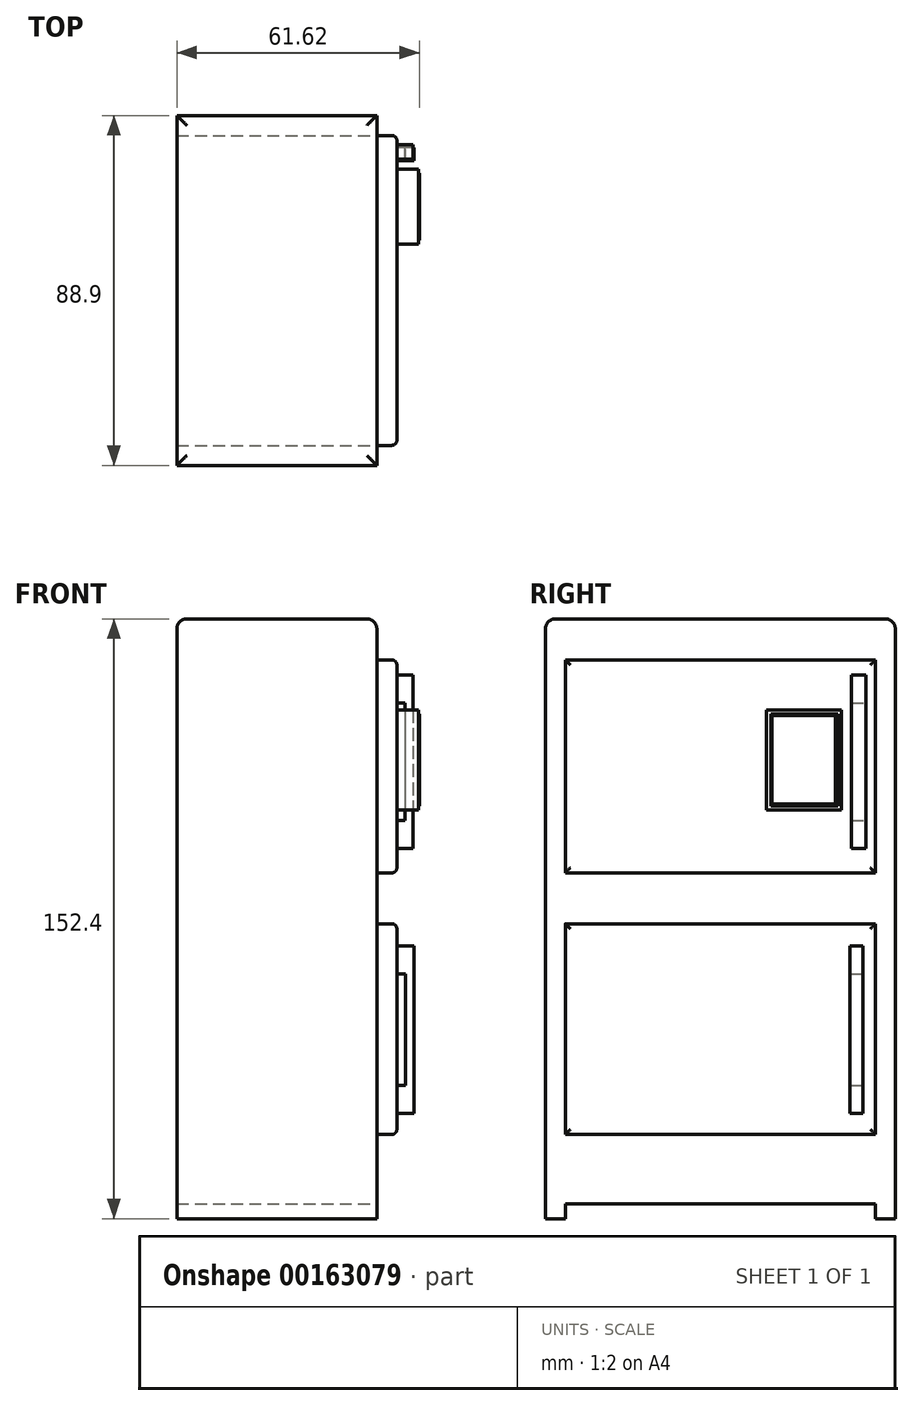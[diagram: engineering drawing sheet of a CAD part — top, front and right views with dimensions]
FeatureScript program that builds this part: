
annotation { "Feature Type Name" : "Feature", "Feature Type Description" : "" }
export const myFeature = defineFeature(function(context is Context, id is Id, definition is map)
    precondition{}
    {
        {
            var Q0;
            Q0=qCreatedBy(makeId("Top.planeOp"),FACE);
            var sketch = newSketch(context, id + "F0", { "sketchPlane" : qUnion([Q0])});
            skLineSegment(sketch, "E0.bottom", {"start": v(0, 0) * mm, "end": v(50.8, 0) * mm});
            skLineSegment(sketch, "E0.top", {"start": v(0, -88.9) * mm, "end": v(50.8, -88.9) * mm});
            skLineSegment(sketch, "E0.left", {"start": v(0, 0) * mm, "end": v(0, -88.9) * mm});
            skLineSegment(sketch, "E0.right", {"start": v(50.8, 0) * mm, "end": v(50.8, -88.9) * mm});
            skSolve(sketch);
        }
        {
            var Q0;
            Q0=makeQuery(id+"F0.imprint","IMPRINT",FACE,{"disambiguationData":[TD([[makeQuery(id+"F0.imprint","IMPRINT",EDGE,{"derivedFrom":sQuery(id+"F0.wireOp",EDGE,"E0.bottom")}),-1.0]])]});
            extrude(context, id + "F1", {"entities" : qUnion([Q0]), "depth" : 152.4 * mm});
        }
        {
            var Q0;
            Q0=makeQuery(id+"F1.opExtrude","CAP_EDGE",EDGE,{"disambiguationData":[OSD([sQuery(id+"F0.wireOp",EDGE,"E0.right")])],"isStart":false});
            var Q1;
            Q1=makeQuery(id+"F1.opExtrude","CAP_EDGE",EDGE,{"disambiguationData":[OSD([sQuery(id+"F0.wireOp",EDGE,"E0.top")])],"isStart":false});
            var Q2;
            Q2=makeQuery(id+"F1.opExtrude","CAP_EDGE",EDGE,{"disambiguationData":[OSD([sQuery(id+"F0.wireOp",EDGE,"E0.bottom")])],"isStart":false});
            var Q3;
            Q3=makeQuery(id+"F1.opExtrude","CAP_EDGE",EDGE,{"disambiguationData":[OSD([sQuery(id+"F0.wireOp",EDGE,"E0.left")])],"isStart":false});
            fillet(context, id + "F2", {"entities" : qUnion([Q0, Q1, Q2, Q3]), "radius" : 2.54 * mm, "tangentPropagation" : true, "allowEdgeOverflow" : false});
        }
        {
            var Q0;
            Q0=makeQuery(id+"F1.opExtrude","SWEPT_FACE",FACE,{"disambiguationData":[OSD([sQuery(id+"F0.wireOp",EDGE,"E0.right")])]});
            var sketch = newSketch(context, id + "F3", { "sketchPlane" : qUnion([Q0])});
            skLineSegment(sketch, "E1.bottom", {"start": v(-83.82, 141.97) * mm, "end": v(-5.08, 141.97) * mm});
            skLineSegment(sketch, "E1.top", {"start": v(-83.82, 87.87) * mm, "end": v(-5.08, 87.87) * mm});
            skLineSegment(sketch, "E1.left", {"start": v(-83.82, 141.97) * mm, "end": v(-83.82, 87.87) * mm});
            skLineSegment(sketch, "E1.right", {"start": v(-5.08, 141.97) * mm, "end": v(-5.08, 87.87) * mm});
            skPoint(sketch, "E2.firstSnap0", {"position": v(0, 74.93) * mm});
            skLineSegment(sketch, "E2.bottom", {"start": v(-5.08, 74.93) * mm, "end": v(-83.82, 74.93) * mm});
            skLineSegment(sketch, "E2.top", {"start": v(-5.08, 21.4) * mm, "end": v(-83.82, 21.4) * mm});
            skLineSegment(sketch, "E2.left", {"start": v(-5.08, 74.93) * mm, "end": v(-5.08, 21.4) * mm});
            skLineSegment(sketch, "E2.right", {"start": v(-83.82, 74.93) * mm, "end": v(-83.82, 21.4) * mm});
            skSolve(sketch);
        }
        {
            var Q0;
            Q0 = qSketchRegion(id + "F3", true);
            extrude(context, id + "F4", {"entities" : qUnion([Q0]), "operationType" : NewBodyOperationType.ADD, "depth" : 5.08 * mm});
        }
        {
            var Q0;
            Q0=makeQuery(id+"F1.opExtrude","SWEPT_FACE",FACE,{"disambiguationData":[OSD([sQuery(id+"F0.wireOp",EDGE,"E0.right")])]});
            var sketch = newSketch(context, id + "F5", { "sketchPlane" : qUnion([Q0])});
            skLineSegment(sketch, "E3.bottom", {"start": v(-83.82, 0) * mm, "end": v(-5.08, 0) * mm});
            skLineSegment(sketch, "E3.top", {"start": v(-83.82, 3.81) * mm, "end": v(-5.08, 3.81) * mm});
            skLineSegment(sketch, "E3.left", {"start": v(-83.82, 0) * mm, "end": v(-83.82, 3.8) * mm});
            skLineSegment(sketch, "E3.right", {"start": v(-5.08, 0) * mm, "end": v(-5.08, 3.81) * mm});
            skSolve(sketch);
        }
        {
            var Q0;
            Q0=makeQuery(id+"F5.imprint","IMPRINT",FACE,{"disambiguationData":[TD([[makeQuery(id+"F5.imprint","IMPRINT",EDGE,{"derivedFrom":sQuery(id+"F5.wireOp",EDGE,"E3.bottom")}),-1.0]])]});
            extrude(context, id + "F6", {"entities" : qUnion([Q0]), "operationType" : NewBodyOperationType.REMOVE, "endBound" : BoundingType.THROUGH_ALL, "oppositeDirection" : true, "depth" : 25.4 * mm});
        }
        {
            var Q0;
            Q0=makeQuery(id+"F4.opExtrude","CAP_FACE",FACE,{"disambiguationData":[OSD([sQuery(id+"F3.wireOp",EDGE,"E1.bottom"),sQuery(id+"F3.wireOp",EDGE,"E1.top"),sQuery(id+"F3.wireOp",EDGE,"E1.left"),sQuery(id+"F3.wireOp",EDGE,"E1.right")])],"isStart":false});
            var sketch = newSketch(context, id + "F7", { "sketchPlane" : qUnion([Q0])});
            skLineSegment(sketch, "E4.bottom", {"start": v(-32.76, 129.27) * mm, "end": v(-13.7, 129.27) * mm});
            skLineSegment(sketch, "E4.top", {"start": v(-32.76, 103.87) * mm, "end": v(-13.7, 103.87) * mm});
            skLineSegment(sketch, "E4.left", {"start": v(-32.76, 129.27) * mm, "end": v(-32.76, 103.87) * mm});
            skLineSegment(sketch, "E4.right", {"start": v(-13.7, 129.27) * mm, "end": v(-13.7, 103.87) * mm});
            skSolve(sketch);
        }
        {
            var Q0;
            Q0=makeQuery(id+"F7.imprint","IMPRINT",FACE,{"disambiguationData":[TD([[makeQuery(id+"F7.imprint","IMPRINT",EDGE,{"derivedFrom":sQuery(id+"F7.wireOp",EDGE,"E4.bottom")}),-1.0]])]});
            extrude(context, id + "F8", {"entities" : qUnion([Q0]), "depth" : 3.8 * mm});
        }
        {
            var Q0;
            Q0=makeQuery(id+"F4.opExtrude","CAP_EDGE",EDGE,{"disambiguationData":[OSD([sQuery(id+"F3.wireOp",EDGE,"E2.bottom")])],"isStart":false});
            var Q1;
            Q1=makeQuery(id+"F4.opExtrude","CAP_EDGE",EDGE,{"disambiguationData":[OSD([sQuery(id+"F3.wireOp",EDGE,"E2.right")])],"isStart":false});
            var Q2;
            Q2=makeQuery(id+"F4.opExtrude","CAP_EDGE",EDGE,{"disambiguationData":[OSD([sQuery(id+"F3.wireOp",EDGE,"E2.top")])],"isStart":false});
            var Q3;
            Q3=makeQuery(id+"F4.opExtrude","CAP_EDGE",EDGE,{"disambiguationData":[OSD([sQuery(id+"F3.wireOp",EDGE,"E2.left")])],"isStart":false});
            var Q4;
            Q4=makeQuery(id+"F4.opExtrude","CAP_EDGE",EDGE,{"disambiguationData":[OSD([sQuery(id+"F3.wireOp",EDGE,"E1.right")])],"isStart":false});
            var Q5;
            Q5=makeQuery(id+"F4.opExtrude","CAP_EDGE",EDGE,{"disambiguationData":[OSD([sQuery(id+"F3.wireOp",EDGE,"E1.top")])],"isStart":false});
            var Q6;
            Q6=makeQuery(id+"F4.opExtrude","CAP_EDGE",EDGE,{"disambiguationData":[OSD([sQuery(id+"F3.wireOp",EDGE,"E1.left")])],"isStart":false});
            var Q7;
            Q7=makeQuery(id+"F4.opExtrude","CAP_EDGE",EDGE,{"disambiguationData":[OSD([sQuery(id+"F3.wireOp",EDGE,"E1.bottom")])],"isStart":false});
            fillet(context, id + "F9", {"entities" : qUnion([Q0, Q1, Q2, Q3, Q4, Q5, Q6, Q7]), "radius" : 1.27 * mm, "tangentPropagation" : true, "allowEdgeOverflow" : false});
        }
        {
            var Q0;
            Q0=makeQuery(id+"F4.opExtrude","CAP_FACE",FACE,{"disambiguationData":[OSD([sQuery(id+"F3.wireOp",EDGE,"E1.bottom"),sQuery(id+"F3.wireOp",EDGE,"E1.top"),sQuery(id+"F3.wireOp",EDGE,"E1.left"),sQuery(id+"F3.wireOp",EDGE,"E1.right")])],"isStart":false});
            var sketch = newSketch(context, id + "F10", { "sketchPlane" : qUnion([Q0])});
            skLineSegment(sketch, "E5.bottom", {"start": v(-11.16, 101.19) * mm, "end": v(-7.48, 101.19) * mm});
            skLineSegment(sketch, "E5.top", {"start": v(-11.16, 94.06) * mm, "end": v(-7.48, 94.06) * mm});
            skLineSegment(sketch, "E5.left", {"start": v(-11.16, 101.19) * mm, "end": v(-11.16, 94.06) * mm});
            skLineSegment(sketch, "E5.right", {"start": v(-7.48, 101.19) * mm, "end": v(-7.48, 94.06) * mm});
            skLineSegment(sketch, "E6.bottom", {"start": v(-11.16, 131.06) * mm, "end": v(-7.48, 131.06) * mm});
            skLineSegment(sketch, "E6.top", {"start": v(-11.16, 138.18) * mm, "end": v(-7.48, 138.18) * mm});
            skLineSegment(sketch, "E6.left", {"start": v(-11.16, 131.06) * mm, "end": v(-11.16, 138.18) * mm});
            skLineSegment(sketch, "E6.right", {"start": v(-7.48, 131.06) * mm, "end": v(-7.48, 138.18) * mm});
            skSolve(sketch);
        }
        {
            var Q0;
            Q0 = qSketchRegion(id + "F10", true);
            extrude(context, id + "F11", {"entities" : qUnion([Q0]), "operationType" : NewBodyOperationType.ADD, "depth" : 4.06 * mm});
        }
        {
            var Q0;
            Q0=makeQuery(id+"F11.opExtrude","SWEPT_FACE",FACE,{"disambiguationData":[OSD([sQuery(id+"F10.wireOp",EDGE,"E5.bottom")])]});
            var sketch = newSketch(context, id + "F12", { "sketchPlane" : qUnion([Q0])});
            skLineSegment(sketch, "E7", {"start": v(57.91, -11.16) * mm, "end": v(57.91, -7.48) * mm});
            skSolve(sketch);
        }
        {
            var Q0;
            Q0 = qSketchRegion(id + "F12", true);
            var Q1;
            {var subQ0=sQuery(id+"F12.wireOp",EDGE,"E7");Q1=makeQuery(id+"F12.imprint","IMPRINT",FACE,{"disambiguationData":[TD([[makeQuery(id+"F12.imprint","IMPRINT",EDGE,{"derivedFrom":subQ0}),-1.0]])]});}
            extrude(context, id + "F13", {"entities" : qUnion([Q0, Q1]), "operationType" : NewBodyOperationType.ADD, "depth" : 29.95 * mm});
        }
        {
            var Q0;
            Q0=makeQuery(id+"F4.opExtrude","CAP_FACE",FACE,{"disambiguationData":[OSD([sQuery(id+"F3.wireOp",EDGE,"E2.bottom"),sQuery(id+"F3.wireOp",EDGE,"E2.top"),sQuery(id+"F3.wireOp",EDGE,"E2.left"),sQuery(id+"F3.wireOp",EDGE,"E2.right")])],"isStart":false});
            var sketch = newSketch(context, id + "F14", { "sketchPlane" : qUnion([Q0])});
            skLineSegment(sketch, "E8.bottom", {"start": v(-11.52, 69.35) * mm, "end": v(-8.22, 69.35) * mm});
            skLineSegment(sketch, "E8.top", {"start": v(-11.52, 62.23) * mm, "end": v(-8.22, 62.23) * mm});
            skLineSegment(sketch, "E8.left", {"start": v(-11.52, 69.35) * mm, "end": v(-11.52, 62.23) * mm});
            skLineSegment(sketch, "E8.right", {"start": v(-8.22, 69.35) * mm, "end": v(-8.22, 62.23) * mm});
            skLineSegment(sketch, "E9.bottom", {"start": v(-11.52, 33.83) * mm, "end": v(-8.22, 33.83) * mm});
            skLineSegment(sketch, "E9.top", {"start": v(-11.52, 26.71) * mm, "end": v(-8.22, 26.71) * mm});
            skLineSegment(sketch, "E9.left", {"start": v(-11.52, 33.83) * mm, "end": v(-11.52, 26.71) * mm});
            skLineSegment(sketch, "E9.right", {"start": v(-8.22, 33.83) * mm, "end": v(-8.22, 26.71) * mm});
            skSolve(sketch);
        }
        {
            var Q0;
            Q0=makeQuery(id+"F14.imprint","IMPRINT",FACE,{"disambiguationData":[TD([[makeQuery(id+"F14.imprint","IMPRINT",EDGE,{"derivedFrom":sQuery(id+"F14.wireOp",EDGE,"E9.bottom")}),-1.0]])]});
            var Q1;
            Q1=makeQuery(id+"F14.imprint","IMPRINT",FACE,{"disambiguationData":[TD([[makeQuery(id+"F14.imprint","IMPRINT",EDGE,{"derivedFrom":sQuery(id+"F14.wireOp",EDGE,"E8.bottom")}),-1.0]])]});
            extrude(context, id + "F15", {"entities" : qUnion([Q0, Q1]), "operationType" : NewBodyOperationType.ADD, "depth" : 4.32 * mm});
        }
        {
            var Q0;
            Q0=makeQuery(id+"F15.opExtrude","SWEPT_FACE",FACE,{"disambiguationData":[OSD([sQuery(id+"F14.wireOp",EDGE,"E9.bottom")])]});
            var sketch = newSketch(context, id + "F16", { "sketchPlane" : qUnion([Q0])});
            skLineSegment(sketch, "E10", {"start": v(58.04, -11.52) * mm, "end": v(58.04, -8.22) * mm});
            skSolve(sketch);
        }
        {
            var Q0;
            Q0 = qSketchRegion(id + "F16", true);
            var Q1;
            {var subQ0=sQuery(id+"F16.wireOp",EDGE,"E10");Q1=makeQuery(id+"F16.imprint","IMPRINT",FACE,{"disambiguationData":[TD([[makeQuery(id+"F16.imprint","IMPRINT",EDGE,{"derivedFrom":subQ0}),-1.0]])]});}
            extrude(context, id + "F17", {"entities" : qUnion([Q0, Q1]), "operationType" : NewBodyOperationType.ADD, "depth" : 28.7 * mm});
        }
        {
            var Q0;
            Q0=makeQuery(id+"F18aBKbNGDZAuSY_2.boolean.opBoolean","SPLIT",FACE,{"disambiguationData":[TD([makeQuery(id+"F18aBKbNGDZAuSY_2.opExtrude","SWEPT_FACE",FACE,{"disambiguationData":[OSD([sQuery(id+"FCajMzsSz2D8gIR_2.wireOp",EDGE,"IWXxuOSV-3M0q-bglJ-may0-hnqPwJEw6C1w")])]})])],"derivedFrom":makeQuery(id+"F8.opExtrude","CAP_FACE",FACE,{"disambiguationData":[OSD([sQuery(id+"F7.wireOp",EDGE,"E4.bottom"),sQuery(id+"F7.wireOp",EDGE,"E4.top"),sQuery(id+"F7.wireOp",EDGE,"E4.left"),sQuery(id+"F7.wireOp",EDGE,"E4.right")])],"isStart":false})});
            var Q1;
            Q1=makeQuery(id+"F18aBKbNGDZAuSY_2.boolean.opBoolean","SPLIT",FACE,{"disambiguationData":[TD([makeQuery(id+"F18aBKbNGDZAuSY_2.opExtrude","SWEPT_FACE",FACE,{"disambiguationData":[OSD([sQuery(id+"FCajMzsSz2D8gIR_2.wireOp",EDGE,"xjBXNSum-RBOt-ipW7-xFAo-kEtw8g1eUzQt")])]})])],"derivedFrom":makeQuery(id+"F8.opExtrude","CAP_FACE",FACE,{"disambiguationData":[OSD([sQuery(id+"F7.wireOp",EDGE,"E4.bottom"),sQuery(id+"F7.wireOp",EDGE,"E4.top"),sQuery(id+"F7.wireOp",EDGE,"E4.left"),sQuery(id+"F7.wireOp",EDGE,"E4.right")])],"isStart":false})});
            var Q2;
            Q2=makeQuery(id+"F18aBKbNGDZAuSY_2.boolean.opBoolean","SPLIT",FACE,{"disambiguationData":[TD([makeQuery(id+"F18aBKbNGDZAuSY_2.opExtrude","SWEPT_FACE",FACE,{"disambiguationData":[OSD([sQuery(id+"FCajMzsSz2D8gIR_2.wireOp",EDGE,"1UY01zUk-WIDg-BB79-jAAV-RaNE0RWoJxyL")])]})])],"derivedFrom":makeQuery(id+"F8.opExtrude","CAP_FACE",FACE,{"disambiguationData":[OSD([sQuery(id+"F7.wireOp",EDGE,"E4.bottom"),sQuery(id+"F7.wireOp",EDGE,"E4.top"),sQuery(id+"F7.wireOp",EDGE,"E4.left"),sQuery(id+"F7.wireOp",EDGE,"E4.right")])],"isStart":false})});
            var Q3;
            Q3=makeQuery(id+"F18aBKbNGDZAuSY_2.boolean.opBoolean","SPLIT",FACE,{"disambiguationData":[TD([makeQuery(id+"F18aBKbNGDZAuSY_2.opExtrude","SWEPT_FACE",FACE,{"disambiguationData":[OSD([sQuery(id+"FCajMzsSz2D8gIR_2.wireOp",EDGE,"E8dGmLqW-HGx9-mBVG-wVn0-xfvv8hPmQ4S1")])]})])],"derivedFrom":makeQuery(id+"F8.opExtrude","CAP_FACE",FACE,{"disambiguationData":[OSD([sQuery(id+"F7.wireOp",EDGE,"E4.bottom"),sQuery(id+"F7.wireOp",EDGE,"E4.top"),sQuery(id+"F7.wireOp",EDGE,"E4.left"),sQuery(id+"F7.wireOp",EDGE,"E4.right")])],"isStart":false})});
            extrude(context, id + "F18", {"entities" : qUnion([Q0, Q1, Q2, Q3]), "operationType" : NewBodyOperationType.ADD, "depth" : 1.7 * mm});
        }
        {
            var Q0;
            Q0=makeQuery(id+"F18.opExtrude","CAP_FACE",FACE,{"disambiguationData":[OSD([sQuery(id+"F7.wireOp",EDGE,"E4.bottom"),sQuery(id+"F7.wireOp",EDGE,"E4.top"),sQuery(id+"F7.wireOp",EDGE,"E4.left"),sQuery(id+"F7.wireOp",EDGE,"E4.right")])],"isStart":false});
            var sketch = newSketch(context, id + "F19", { "sketchPlane" : qUnion([Q0])});
            skLineSegment(sketch, "E11.bottom", {"start": v(-31.65, 128.26) * mm, "end": v(-14.64, 128.26) * mm});
            skLineSegment(sketch, "E11.top", {"start": v(-31.65, 104.86) * mm, "end": v(-14.64, 104.86) * mm});
            skLineSegment(sketch, "E11.left", {"start": v(-31.65, 128.26) * mm, "end": v(-31.65, 104.86) * mm});
            skLineSegment(sketch, "E11.right", {"start": v(-14.64, 128.26) * mm, "end": v(-14.64, 104.86) * mm});
            skSolve(sketch);
        }
        {
            var Q0;
            Q0 = qSketchRegion(id + "F19", true);
            extrude(context, id + "F20", {"entities" : qUnion([Q0]), "depth" : 0.03 * mm});
        }
        {
            var Q0;
            Q0=makeQuery(id+"F20.opExtrude","CAP_FACE",FACE,{"disambiguationData":[OSD([sQuery(id+"F19.wireOp",EDGE,"E11.bottom"),sQuery(id+"F19.wireOp",EDGE,"E11.top"),sQuery(id+"F19.wireOp",EDGE,"E11.left"),sQuery(id+"F19.wireOp",EDGE,"E11.right")])],"isStart":false});
            var sketch = newSketch(context, id + "F21", { "sketchPlane" : qUnion([Q0])});
            skLineSegment(sketch, "E12.bottom", {"start": v(-31.3, 127.78) * mm, "end": v(-15.17, 127.78) * mm});
            skLineSegment(sketch, "E12.top", {"start": v(-31.3, 105.3) * mm, "end": v(-15.17, 105.3) * mm});
            skLineSegment(sketch, "E12.left", {"start": v(-31.3, 127.78) * mm, "end": v(-31.3, 105.3) * mm});
            skLineSegment(sketch, "E12.right", {"start": v(-15.17, 127.78) * mm, "end": v(-15.17, 105.3) * mm});
            skSolve(sketch);
        }
        {
            var Q0;
            Q0=makeQuery(id+"F21.imprint","IMPRINT",FACE,{"disambiguationData":[TD([[makeQuery(id+"F21.imprint","IMPRINT",EDGE,{"derivedFrom":sQuery(id+"F21.wireOp",EDGE,"E12.bottom")}),1.0]])]});
            extrude(context, id + "F22", {"entities" : qUnion([Q0]), "depth" : 0.2 * mm});
        }
    });
